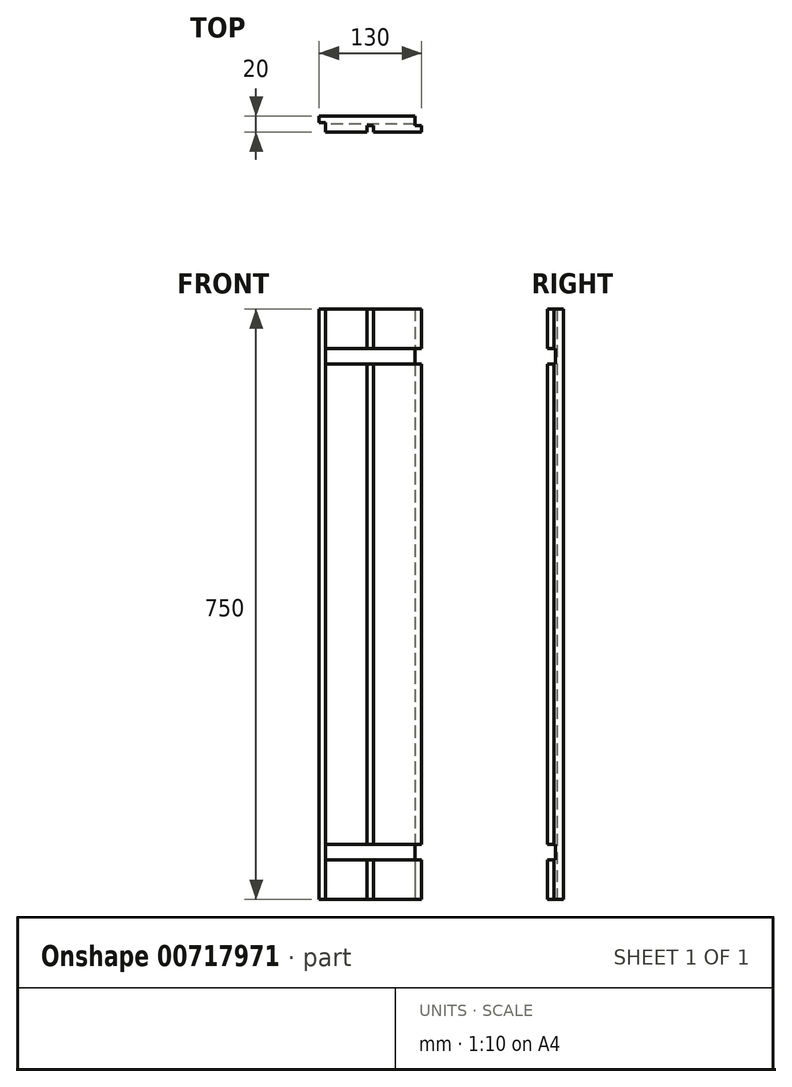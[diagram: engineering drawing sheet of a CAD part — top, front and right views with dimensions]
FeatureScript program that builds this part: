
annotation { "Feature Type Name" : "Feature", "Feature Type Description" : "" }
export const myFeature = defineFeature(function(context is Context, id is Id, definition is map)
    precondition{}
    {
        {
            var Q0;
            Q0=qCreatedBy(makeId("Front.planeOp"),FACE);
            var sketch = newSketch(context, id + "F0", { "sketchPlane" : qUnion([Q0])});
            skLineSegment(sketch, "E0.bottom", {"start": v(-374.72, 484.48) * mm, "end": v(-244.72, 484.48) * mm});
            skLineSegment(sketch, "E0.top", {"start": v(-374.72, -265.52) * mm, "end": v(-244.72, -265.52) * mm});
            skLineSegment(sketch, "E0.left", {"start": v(-374.72, 484.48) * mm, "end": v(-374.72, -265.52) * mm});
            skLineSegment(sketch, "E0.right", {"start": v(-244.72, 484.48) * mm, "end": v(-244.72, -265.52) * mm});
            skSolve(sketch);
        }
        {
            var Q0;
            Q0=makeQuery(id+"F0.imprint","IMPRINT",FACE,{"disambiguationData":[TD([[makeQuery(id+"F0.imprint","IMPRINT",EDGE,{"derivedFrom":sQuery(id+"F0.wireOp",EDGE,"E0.bottom")}),-1.0]])]});
            extrude(context, id + "F1", {"entities" : qUnion([Q0]), "oppositeDirection" : true, "depth" : 20 * mm, "offsetDistance" : 25.4 * mm});
        }
        {
            var Q0;
            Q0=makeQuery(id+"F1.opExtrude","CAP_FACE",FACE,{"disambiguationData":[OSD([sQuery(id+"F0.wireOp",EDGE,"E0.bottom"),sQuery(id+"F0.wireOp",EDGE,"E0.top"),sQuery(id+"F0.wireOp",EDGE,"E0.left"),sQuery(id+"F0.wireOp",EDGE,"E0.right")])],"isStart":true});
            var sketch = newSketch(context, id + "F2", { "sketchPlane" : qUnion([Q0])});
            skLineSegment(sketch, "E1.bottom", {"start": v(-313.72, 484.48) * mm, "end": v(-305.72, 484.48) * mm});
            skLineSegment(sketch, "E1.top", {"start": v(-313.72, -975.52) * mm, "end": v(-305.72, -975.52) * mm});
            skLineSegment(sketch, "E1.left", {"start": v(-313.72, 484.48) * mm, "end": v(-313.72, -975.52) * mm});
            skLineSegment(sketch, "E1.right", {"start": v(-305.72, 484.48) * mm, "end": v(-305.72, -975.52) * mm});
            skSolve(sketch);
        }
        {
            var Q0;
            Q0=makeQuery(id+"F2.imprint","IMPRINT",FACE,{"disambiguationData":[TD([[makeQuery(id+"F2.imprint","IMPRINT",EDGE,{"derivedFrom":sQuery(id+"F2.wireOp",EDGE,"E1.bottom")}),-1.0]])]});
            extrude(context, id + "F3", {"entities" : qUnion([Q0]), "operationType" : NewBodyOperationType.REMOVE, "oppositeDirection" : true, "depth" : 8 * mm, "offsetDistance" : 25.4 * mm});
        }
        {
            var Q0;
            {var subQ0=sQuery(id+"F0.wireOp",EDGE,"E0.bottom");var subQ1=sQuery(id+"F0.wireOp",EDGE,"E0.top");var subQ2=sQuery(id+"F0.wireOp",EDGE,"E0.left");Q0=makeQuery(id+"F3.boolean.opBoolean","SPLIT",FACE,{"disambiguationData":[TD([makeQuery(id+"F1.opExtrude","SWEPT_FACE",FACE,{"disambiguationData":[OSD([subQ2])]})])],"derivedFrom":makeQuery(id+"F1.opExtrude","CAP_FACE",FACE,{"disambiguationData":[OSD([subQ0,subQ1,subQ2,sQuery(id+"F0.wireOp",EDGE,"E0.right")])],"isStart":true})});}
            var sketch = newSketch(context, id + "F4", { "sketchPlane" : qUnion([Q0])});
            skLineSegment(sketch, "E2.bottom", {"start": v(-374.72, 484.48) * mm, "end": v(-366.72, 484.48) * mm});
            skLineSegment(sketch, "E2.top", {"start": v(-374.72, -975.52) * mm, "end": v(-366.72, -975.52) * mm});
            skLineSegment(sketch, "E2.left", {"start": v(-374.72, 484.48) * mm, "end": v(-374.72, -975.52) * mm});
            skLineSegment(sketch, "E2.right", {"start": v(-366.72, 484.48) * mm, "end": v(-366.72, -975.52) * mm});
            skSolve(sketch);
        }
        {
            var Q0;
            Q0=makeQuery(id+"F4.imprint","IMPRINT",FACE,{"disambiguationData":[TD([[makeQuery(id+"F4.imprint","IMPRINT",EDGE,{"derivedFrom":sQuery(id+"F4.wireOp",EDGE,"E2.bottom")}),-1.0]])]});
            extrude(context, id + "F5", {"entities" : qUnion([Q0]), "operationType" : NewBodyOperationType.REMOVE, "oppositeDirection" : true, "depth" : 12 * mm, "offsetDistance" : 25.4 * mm});
        }
        {
            var Q0;
            Q0=makeQuery(id+"F1.opExtrude","CAP_FACE",FACE,{"disambiguationData":[OSD([sQuery(id+"F0.wireOp",EDGE,"E0.bottom"),sQuery(id+"F0.wireOp",EDGE,"E0.top"),sQuery(id+"F0.wireOp",EDGE,"E0.left"),sQuery(id+"F0.wireOp",EDGE,"E0.right")])],"isStart":false});
            var sketch = newSketch(context, id + "F6", { "sketchPlane" : qUnion([Q0])});
            skLineSegment(sketch, "E3.bottom", {"start": v(244.72, 484.48) * mm, "end": v(252.72, 484.48) * mm});
            skLineSegment(sketch, "E3.top", {"start": v(244.72, -975.52) * mm, "end": v(252.72, -975.52) * mm});
            skLineSegment(sketch, "E3.left", {"start": v(244.72, 484.48) * mm, "end": v(244.72, -975.52) * mm});
            skLineSegment(sketch, "E3.right", {"start": v(252.72, 484.48) * mm, "end": v(252.72, -975.52) * mm});
            skSolve(sketch);
        }
        {
            var Q0;
            Q0=makeQuery(id+"F6.imprint","IMPRINT",FACE,{"disambiguationData":[TD([[makeQuery(id+"F6.imprint","IMPRINT",EDGE,{"derivedFrom":sQuery(id+"F6.wireOp",EDGE,"E3.bottom")}),1.0]])]});
            extrude(context, id + "F7", {"entities" : qUnion([Q0]), "operationType" : NewBodyOperationType.REMOVE, "oppositeDirection" : true, "depth" : 12 * mm, "offsetDistance" : 25.4 * mm});
        }
        {
            var Q0;
            Q0=makeQuery(id+"F5.boolean.opBoolean","COPY",FACE,{"derivedFrom":makeQuery(id+"F5.opExtrude","SWEPT_FACE",FACE,{"disambiguationData":[OSD([sQuery(id+"F4.wireOp",EDGE,"E2.right")])]})});
            var sketch = newSketch(context, id + "F8", { "sketchPlane" : qUnion([Q0])});
            skLineSegment(sketch, "E4.bottom", {"start": v(0, 434.48) * mm, "end": v(-10, 434.48) * mm});
            skLineSegment(sketch, "E4.top", {"start": v(0, 414.48) * mm, "end": v(-10, 414.48) * mm});
            skLineSegment(sketch, "E4.left", {"start": v(0, 434.48) * mm, "end": v(0, 414.48) * mm});
            skLineSegment(sketch, "E4.right", {"start": v(-10, 434.48) * mm, "end": v(-10, 414.48) * mm});
            skLineSegment(sketch, "E5.bottom", {"start": v(0, -215.52) * mm, "end": v(-10, -215.52) * mm});
            skLineSegment(sketch, "E5.top", {"start": v(0, -195.52) * mm, "end": v(-10, -195.52) * mm});
            skLineSegment(sketch, "E5.left", {"start": v(0, -215.52) * mm, "end": v(0, -195.52) * mm});
            skLineSegment(sketch, "E5.right", {"start": v(-10, -215.52) * mm, "end": v(-10, -195.52) * mm});
            skSolve(sketch);
        }
        {
            var Q0;
            Q0=makeQuery(id+"F8.imprint","IMPRINT",FACE,{"disambiguationData":[TD([[makeQuery(id+"F8.imprint","IMPRINT",EDGE,{"derivedFrom":sQuery(id+"F8.wireOp",EDGE,"E5.bottom")}),-1.0]])]});
            var Q1;
            Q1=makeQuery(id+"F8.imprint","IMPRINT",FACE,{"disambiguationData":[TD([[makeQuery(id+"F8.imprint","IMPRINT",EDGE,{"derivedFrom":sQuery(id+"F8.wireOp",EDGE,"E4.bottom")}),1.0]])]});
            extrude(context, id + "F9", {"entities" : qUnion([Q0, Q1]), "operationType" : NewBodyOperationType.REMOVE, "oppositeDirection" : true, "depth" : 130 * mm, "offsetDistance" : 25 * mm});
        }
    });
